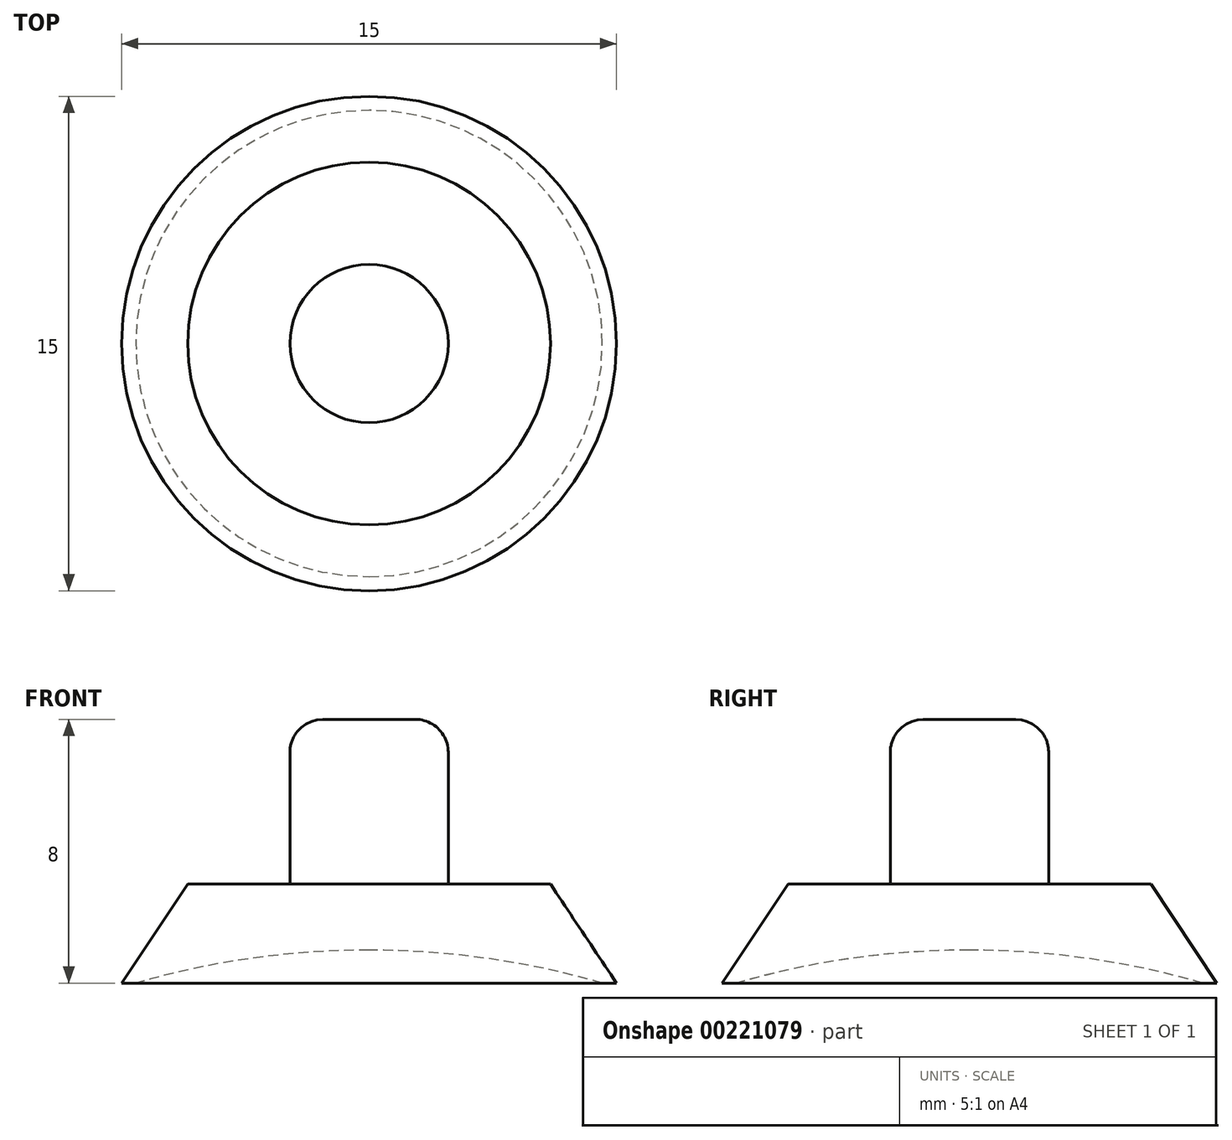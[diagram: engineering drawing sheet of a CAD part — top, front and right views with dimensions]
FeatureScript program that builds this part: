
annotation { "Feature Type Name" : "Feature", "Feature Type Description" : "" }
export const myFeature = defineFeature(function(context is Context, id is Id, definition is map)
    precondition{}
    {
        {
            var Q0;
            Q0=qCreatedBy(makeId("Top.planeOp"),FACE);
            var sketch = newSketch(context, id + "F0", { "sketchPlane" : qUnion([Q0])});
            skCircle(sketch, "E0", {"center": v(0, 0) * mm, "radius": 7.5 * mm});
            skSolve(sketch);
        }
        {
            var Q0;
            Q0 = qSketchRegion(id + "F0", true);
            extrude(context, id + "F1", {"entities" : qUnion([Q0]), "depth" : 3 * mm});
        }
        {
            var Q0;
            Q0=makeQuery(id+"F1.opExtrude","CAP_EDGE",EDGE,{"disambiguationData":[OSD([sQuery(id+"F0.wireOp",EDGE,"E0")])],"isStart":false});
            chamfer(context, id + "F2", {"entities" : qUnion([Q0]), "chamferType" : ChamferType.TWO_OFFSETS, "width1" : 2 * mm, "oppositeDirection" : false, "width2" : 3 * mm});
        }
        {
            var Q0;
            Q0=makeQuery(id+"F1.opExtrude","CAP_FACE",FACE,{"disambiguationData":[OSD([sQuery(id+"F0.wireOp",EDGE,"E0")])],"isStart":false});
            var sketch = newSketch(context, id + "F3", { "sketchPlane" : qUnion([Q0])});
            skCircle(sketch, "E1", {"center": v(0, 0) * mm, "radius": 2.4 * mm});
            skCircle(sketch, "E2", {"center": v(0, 0) * mm, "radius": 6.04 * mm});
            skSolve(sketch);
        }
        {
            var Q0;
            Q0=makeQuery(id+"F3.imprint","IMPRINT",FACE,{"disambiguationData":[TD([[makeQuery(id+"F3.imprint","IMPRINT",EDGE,{"derivedFrom":sQuery(id+"F3.wireOp",EDGE,"E1")}),1.0]])]});
            extrude(context, id + "F4", {"entities" : qUnion([Q0]), "operationType" : NewBodyOperationType.ADD, "depth" : 5 * mm});
        }
        {
            var Q0;
            Q0=makeQuery(id+"F4.opExtrude","CAP_EDGE",EDGE,{"disambiguationData":[OSD([sQuery(id+"F3.wireOp",EDGE,"E1")])],"isStart":false});
            var Q1;
            Q1=makeQuery(id+"F4.opExtrude","CAP_EDGE",EDGE,{"disambiguationData":[OSD([sQuery(id+"F3.wireOp",EDGE,"E1")])],"isStart":true});
            fillet(context, id + "F5", {"entities" : qUnion([Q0, Q1]), "radius" : 1 * mm, "tangentPropagation" : true, "allowEdgeOverflow" : false});
        }
        {
            var Q0;
            Q0=qCreatedBy(makeId("Right.planeOp"),FACE);
            var sketch = newSketch(context, id + "F6", { "sketchPlane" : qUnion([Q0])});
            skArc(sketch, "E3", {"start": v(0, 1) * mm, "mid": v(-18.03, -6.47) * mm, "end": v(-25.5, -24.5) * mm});
            skLineSegment(sketch, "E4", {"start": v(0, 0) * mm, "end": v(0, -24.5) * mm});
            skLineSegment(sketch, "E5", {"start": v(0, -24.5) * mm, "end": v(-25.5, -24.5) * mm});
            skLineSegment(sketch, "E6", {"start": v(0, 0) * mm, "end": v(0, 1) * mm});
            skSolve(sketch);
        }
        {
            var Q0;
            Q0=makeQuery(id+"F6.imprint","IMPRINT",FACE,{"disambiguationData":[TD([[makeQuery(id+"F6.imprint","IMPRINT",EDGE,{"derivedFrom":sQuery(id+"F6.wireOp",EDGE,"E3")}),1.0]])]});
            var Q1;
            Q1=sQuery(id+"F6.wireOp",EDGE,"E4");
            revolve(context, id + "F7", {"operationType" : NewBodyOperationType.REMOVE, "entities" : qUnion([Q0]), "axis" : qUnion([Q1]), "revolveType" : RevolveType.FULL, "oppositeDirection" : true});
        }
    });
